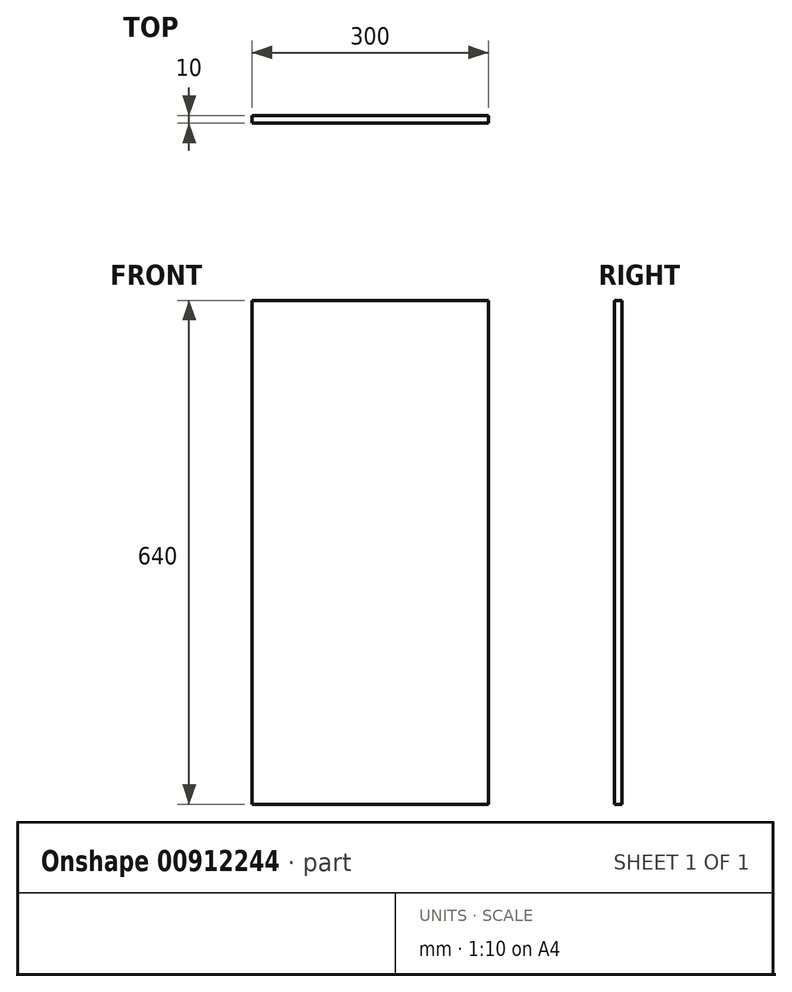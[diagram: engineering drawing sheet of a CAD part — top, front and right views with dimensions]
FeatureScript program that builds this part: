
annotation { "Feature Type Name" : "Feature", "Feature Type Description" : "" }
export const myFeature = defineFeature(function(context is Context, id is Id, definition is map)
    precondition{}
    {
        {
            var Q0;
            Q0=qCreatedBy(makeId("Front.planeOp"),FACE);
            var sketch = newSketch(context, id + "F0", { "sketchPlane" : qUnion([Q0])});
            skLineSegment(sketch, "E0.bottom", {"start": v(-165.88, 287.88) * mm, "end": v(134.12, 287.88) * mm});
            skLineSegment(sketch, "E0.top", {"start": v(-165.88, -352.12) * mm, "end": v(134.12, -352.12) * mm});
            skLineSegment(sketch, "E0.left", {"start": v(-165.88, 287.88) * mm, "end": v(-165.88, -352.12) * mm});
            skLineSegment(sketch, "E0.right", {"start": v(134.12, 287.88) * mm, "end": v(134.12, -352.12) * mm});
            skSolve(sketch);
        }
        {
            var Q0;
            Q0 = qSketchRegion(id + "F0", true);
            extrude(context, id + "F1", {"entities" : qUnion([Q0]), "depth" : 10 * mm, "offsetDistance" : 25 * mm});
        }
    });
